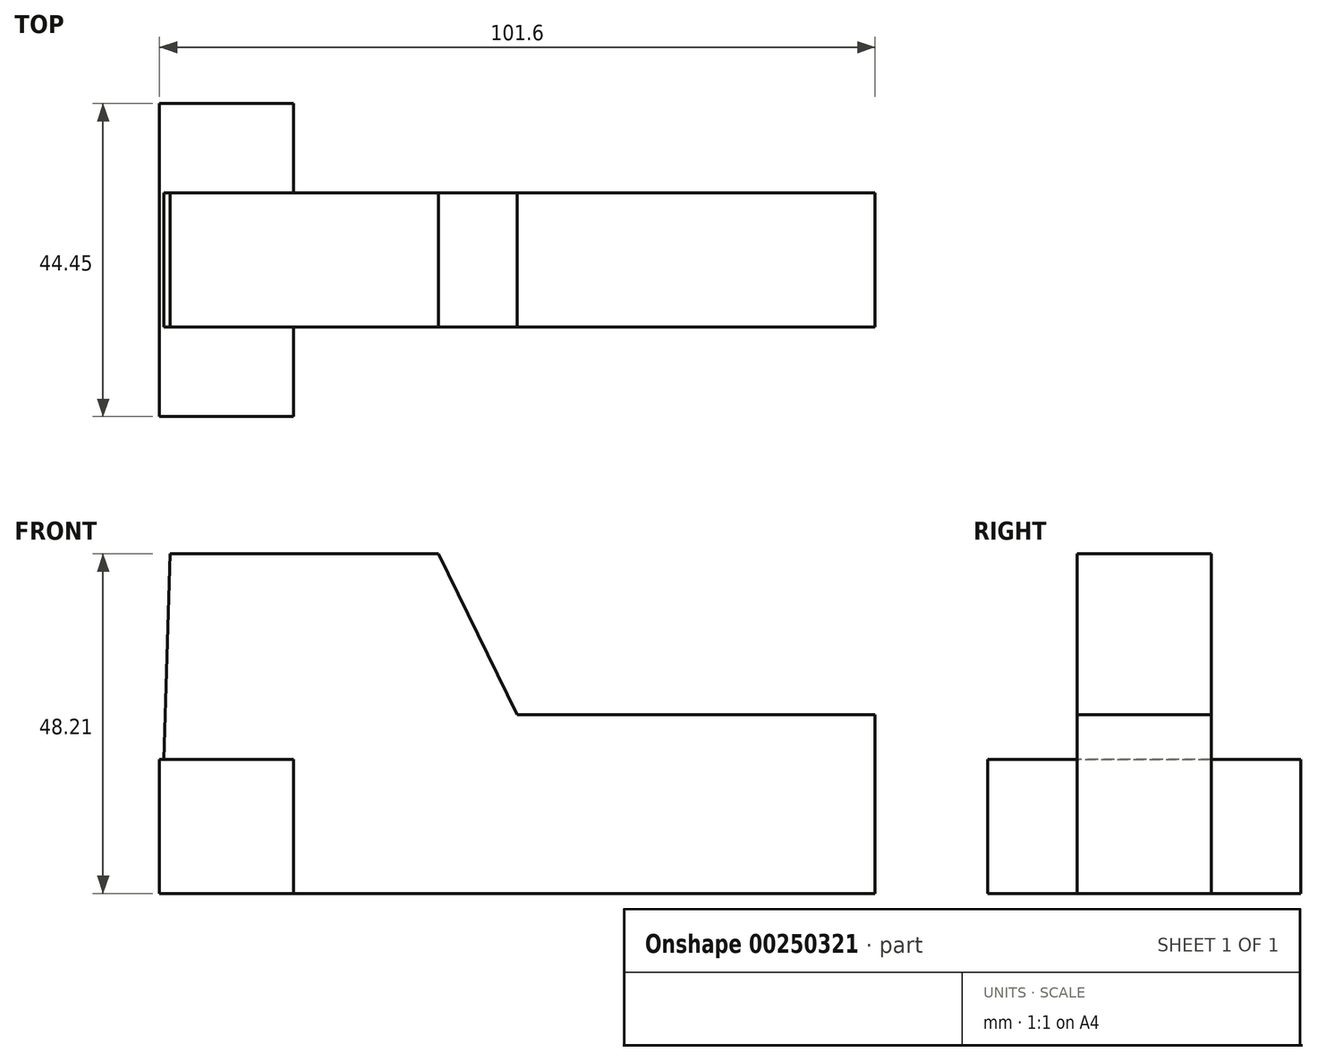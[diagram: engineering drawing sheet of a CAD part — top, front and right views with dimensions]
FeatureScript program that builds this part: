
annotation { "Feature Type Name" : "Feature", "Feature Type Description" : "" }
export const myFeature = defineFeature(function(context is Context, id is Id, definition is map)
    precondition{}
    {
        {
            var Q0;
            Q0=qCreatedBy(makeId("Front.planeOp"),FACE);
            var sketch = newSketch(context, id + "F0", { "sketchPlane" : qUnion([Q0])});
            skLineSegment(sketch, "E0", {"start": v(0, 0) * mm, "end": v(101.6, 0) * mm});
            skLineSegment(sketch, "E1", {"start": v(101.6, 25.4) * mm, "end": v(101.6, 0) * mm});
            skLineSegment(sketch, "E2", {"start": v(101.6, 25.4) * mm, "end": v(50.8, 25.4) * mm});
            skLineSegment(sketch, "E3", {"start": v(50.8, 25.4) * mm, "end": v(53.86, 25.4) * mm});
            skLineSegment(sketch, "E4", {"start": v(50.8, 25.4) * mm, "end": v(39.63, 48.21) * mm});
            skLineSegment(sketch, "E5", {"start": v(39.63, 48.21) * mm, "end": v(1.53, 48.21) * mm});
            skLineSegment(sketch, "E6", {"start": v(1.53, 48.21) * mm, "end": v(0, 0) * mm});
            skSolve(sketch);
        }
        {
            var Q0;
            Q0=makeQuery(id+"F0.imprint","IMPRINT",FACE,{"disambiguationData":[TD([[makeQuery(id+"F0.imprint","IMPRINT",EDGE,{"derivedFrom":sQuery(id+"F0.wireOp",EDGE,"E0")}),1.0]])]});
            extrude(context, id + "F1", {"entities" : qUnion([Q0]), "depth" : 19.05 * mm});
        }
        {
            var Q0;
            Q0=qCreatedBy(makeId("Front.planeOp"),FACE);
            var sketch = newSketch(context, id + "F2", { "sketchPlane" : qUnion([Q0])});
            skLineSegment(sketch, "E7.bottom", {"start": v(0, 0) * mm, "end": v(19.05, 0) * mm});
            skLineSegment(sketch, "E7.top", {"start": v(0, 19.05) * mm, "end": v(19.05, 19.05) * mm});
            skLineSegment(sketch, "E7.left", {"start": v(0, 0) * mm, "end": v(0, 19.05) * mm});
            skLineSegment(sketch, "E7.right", {"start": v(19.05, 0) * mm, "end": v(19.05, 19.05) * mm});
            skSolve(sketch);
        }
        {
            var Q0;
            Q0=makeQuery(id+"F2.imprint","IMPRINT",FACE,{"disambiguationData":[TD([[makeQuery(id+"F2.imprint","IMPRINT",EDGE,{"derivedFrom":sQuery(id+"F2.wireOp",EDGE,"E7.bottom")}),1.0]])]});
            extrude(context, id + "F3", {"entities" : qUnion([Q0]), "operationType" : NewBodyOperationType.ADD, "depth" : 31.75 * mm, "hasSecondDirection" : true, "secondDirectionOppositeDirection" : true, "secondDirectionDepth" : 12.7 * mm});
        }
    });
